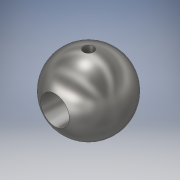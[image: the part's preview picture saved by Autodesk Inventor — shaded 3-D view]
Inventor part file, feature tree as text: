
AUTODESK INVENTOR PART (.ipt)
format: ipt  version: 2017 (Build 210142000, 142)  size: 155,648 bytes
history: native  units: in
note: dims shown in document units (in); Inventor stores cm internally (conversion verified against a paired STEP export)
features: sketch x3, plane x2, extrude x2, revolve x1
ambient origin geometry x8: Origin, YZ Plane, XZ Plane, XY Plane, X Axis, Y Axis, Z Axis, Center Point
bodies: Solid1 (feature_tree)
feature tree (8):
  revolve  "Revolution1"  Angle=90.0deg
  plane  "Work Plane1"
  plane  "Work Plane2"
  extrude  "Extrusion1"  Depth=0.104in
  extrude  "Extrusion2"  Depth=1.0in TaperAngle=0.0deg
  sketch  "Sketch1"  dims[d0=0.75in d1=90.0deg]
  sketch  "Sketch5"  dims[d11=0.375in d19=0.104in]
  sketch  "Sketch6"  dims[d20=0.375in d21=1.0in d22=0.0in d23=0.375in d24=0.295in d25=0.5in d26=0.0in]
